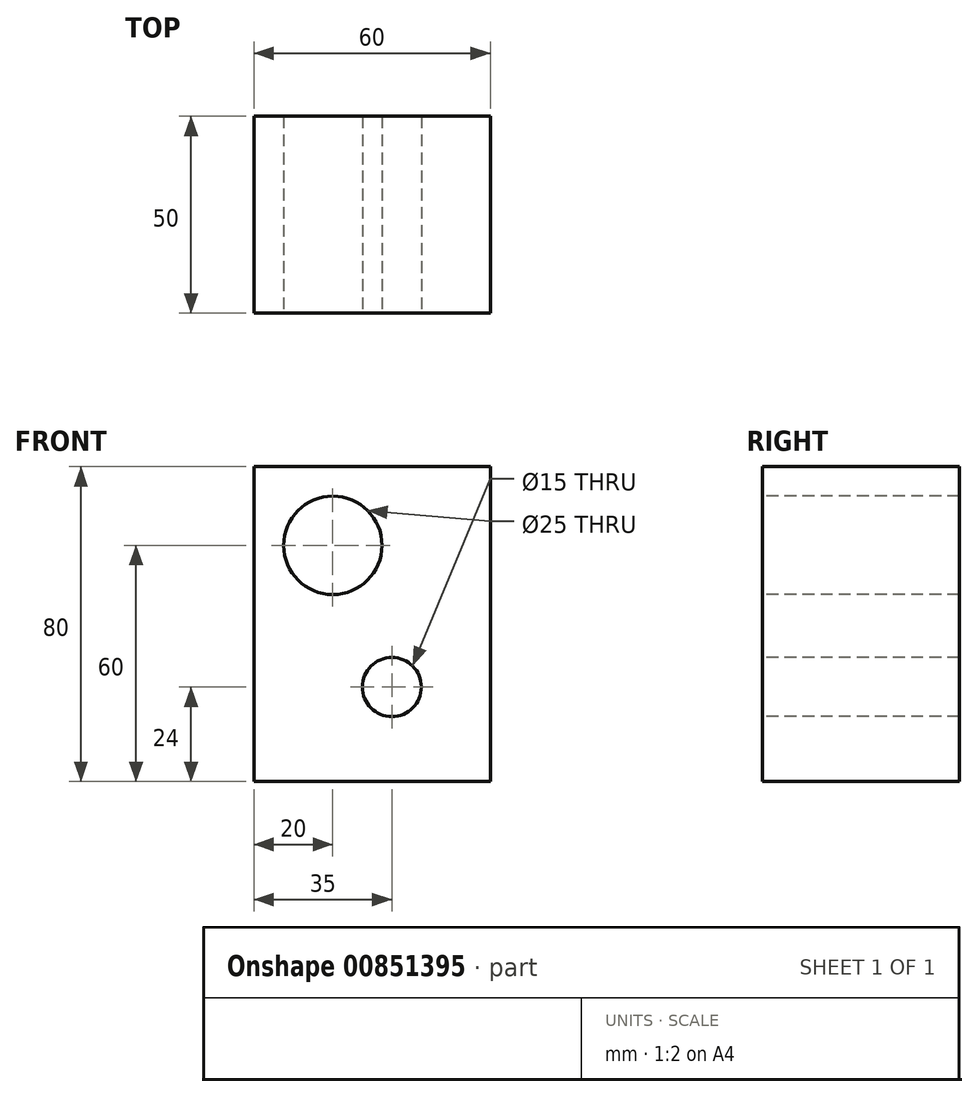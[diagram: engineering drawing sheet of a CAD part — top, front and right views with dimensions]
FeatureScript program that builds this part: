
annotation { "Feature Type Name" : "Feature", "Feature Type Description" : "" }
export const myFeature = defineFeature(function(context is Context, id is Id, definition is map)
    precondition{}
    {
        {
            var Q0;
            Q0=qCreatedBy(makeId("Front.planeOp"),FACE);
            var sketch = newSketch(context, id + "F0", { "sketchPlane" : qUnion([Q0])});
            skLineSegment(sketch, "E0.bottom", {"start": v(-30, 40) * mm, "end": v(30, 40) * mm});
            skLineSegment(sketch, "E0.top", {"start": v(-30, -40) * mm, "end": v(30, -40) * mm});
            skLineSegment(sketch, "E0.left", {"start": v(-30, 40) * mm, "end": v(-30, -40) * mm});
            skLineSegment(sketch, "E0.right", {"start": v(30, 40) * mm, "end": v(30, -40) * mm});
            skPoint(sketch, "E1", {"position": v(-30, 0) * mm});
            skPoint(sketch, "E2", {"position": v(0, 40) * mm});
            skSolve(sketch);
        }
        {
            var Q0;
            Q0=makeQuery(id+"F0.imprint","IMPRINT",FACE,{"disambiguationData":[TD([[makeQuery(id+"F0.imprint","IMPRINT",EDGE,{"derivedFrom":sQuery(id+"F0.wireOp",EDGE,"E0.bottom")}),-1.0]])]});
            extrude(context, id + "F1", {"entities" : qUnion([Q0]), "endBound" : BoundingType.SYMMETRIC, "depth" : 50 * mm, "offsetDistance" : 25 * mm, "hasSecondDirection" : true, "secondDirectionOppositeDirection" : true, "secondDirectionDepth" : 25 * mm});
        }
        {
            var Q0;
            Q0=makeQuery(id+"F1.opExtrude","CAP_FACE",FACE,{"disambiguationData":[OSD([sQuery(id+"F0.wireOp",EDGE,"E0.bottom"),sQuery(id+"F0.wireOp",EDGE,"E0.top"),sQuery(id+"F0.wireOp",EDGE,"E0.left"),sQuery(id+"F0.wireOp",EDGE,"E0.right")])],"isStart":false});
            var sketch = newSketch(context, id + "F2", { "sketchPlane" : qUnion([Q0])});
            skCircle(sketch, "E3", {"center": v(-10, 20) * mm, "radius": 12.5 * mm});
            skCircle(sketch, "E4", {"center": v(5, -16) * mm, "radius": 7.5 * mm});
            skSolve(sketch);
        }
        {
            var Q0;
            Q0 = qSketchRegion(id + "F2", true);
            extrude(context, id + "F3", {"entities" : qUnion([Q0]), "operationType" : NewBodyOperationType.REMOVE, "endBound" : BoundingType.UP_TO_NEXT, "oppositeDirection" : true, "depth" : 25 * mm, "offsetDistance" : 25 * mm});
        }
    });
